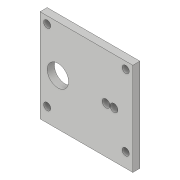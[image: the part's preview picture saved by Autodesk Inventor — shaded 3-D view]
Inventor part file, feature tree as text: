
AUTODESK INVENTOR PART (.ipt)
format: ipt  version: 2019 (Build 230136000, 136)  size: 126,464 bytes
history: native  units: in
note: dims shown in document units (in); Inventor stores cm internally (conversion verified against a paired STEP export)
features: extrude x5, sketch x5
ambient origin geometry x8: Origin, YZ Plane, XZ Plane, XY Plane, X Axis, Y Axis, Z Axis, Center Point
bodies: Solid1 (feature_tree)
feature tree (10):
  extrude  "Extrusion1"  Depth=5.1181in
  extrude  "Extrusion2"  Depth=0.3937in
  extrude  "Extrusion3"  Depth=4.3307in
  extrude  "Extrusion4"  Depth=4.7244in
  extrude  "Extrusion5"  Depth=0.3937in
  sketch  "Sketch1"  dims[d0=5.1181in d1=5.1181in]
  sketch  "Sketch2"  dims[d2=0.3937in d3=0.0in d4=0.3937in]
  sketch  "Sketch3"  dims[d5=4.3307in d6=4.3307in]
  sketch  "Sketch4"  dims[d7=4.3307in d8=4.7244in]
  sketch  "Sketch5"  dims[d9=4.3307in d10=4.3307in d11=0.3937in d12=0.3937in d13=0.3937in d14=0.3937in d15=0.3937in d16=0.3937in d17=0.0in d18=2.5591in d19=1.4764in d20=0.4331in d21=0.3937in d22=0.0in d23=2.5591in d24=0.9843in d25=1.1811in d26=0.3937in d27=0.0in d28=0.9843in d29=0.4331in d30=0.4331in d31=0.0in]
